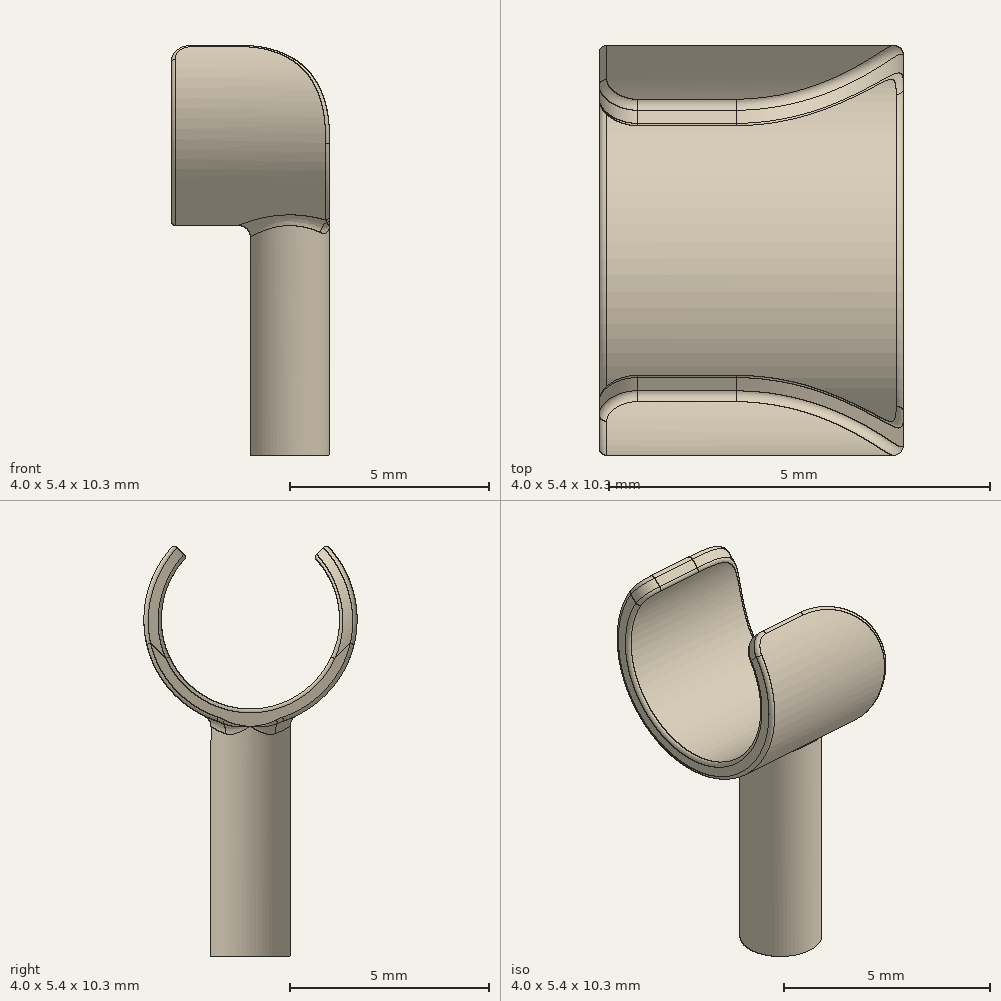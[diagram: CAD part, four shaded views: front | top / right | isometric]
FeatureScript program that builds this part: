
annotation { "Feature Type Name" : "Feature", "Feature Type Description" : "" }
export const myFeature = defineFeature(function(context is Context, id is Id, definition is map)
    precondition{}
    {
        {
            var Q0;
            Q0=qCreatedBy(makeId("Top.planeOp"),FACE);
            var sketch = newSketch(context, id + "F0", { "sketchPlane" : qUnion([Q0])});
            skCircle(sketch, "E0", {"center": v(0, 0) * mm, "radius": 1 * mm});
            skSolve(sketch);
        }
        {
            var Q0;
            Q0=makeQuery(id+"F0.imprint","IMPRINT",FACE,{"disambiguationData":[TD([[makeQuery(id+"F0.imprint","IMPRINT",EDGE,{"derivedFrom":sQuery(id+"F0.wireOp",EDGE,"E0")}),1.0]])]});
            extrude(context, id + "F1", {"entities" : qUnion([Q0]), "depth" : 6 * mm});
        }
        {
            var Q0;
            Q0=qCreatedBy(makeId("Right.planeOp"),FACE);
            cPlane(context, id + "F2", {"entities" : qUnion([Q0]), "cplaneType" : CPlaneType.OFFSET, "offset" : 1 * mm, "width" : 150 * mm, "height" : 150 * mm});
        }
        {
            var Q0;
            Q0=qCreatedBy(id+"F2.planeOp",FACE);
            var sketch = newSketch(context, id + "F3", { "sketchPlane" : qUnion([Q0])});
            skArc(sketch, "E1", {"start": v(-1.6, 10.67) * mm, "mid": v(0, 5.8) * mm, "end": v(1.6, 10.67) * mm});
            skArc(sketch, "E2", {"start": v(-1.6, 10.08) * mm, "mid": v(0, 6.25) * mm, "end": v(1.6, 10.08) * mm});
            skLineSegment(sketch, "E3.0", {"start": v(-1, 6) * mm, "end": v(1, 6) * mm});
            skLineSegment(sketch, "E4", {"start": v(0, 8.5) * mm, "end": v(-2.59, 11.06) * mm});
            skLineSegment(sketch, "E5", {"start": v(0, 8.5) * mm, "end": v(2.69, 11.16) * mm});
            skLineSegment(sketch, "E6", {"start": v(1.6, 10.08) * mm, "end": v(1.6, 10.67) * mm});
            skLineSegment(sketch, "E7", {"start": v(-1.6, 10.08) * mm, "end": v(-1.6, 10.67) * mm});
            skSolve(sketch);
        }
        {
            var Q0;
            {var subQ0=sQuery(id+"F3.wireOp",EDGE,"E2");Q0=makeQuery(id+"F3.imprint","IMPRINT",FACE,{"disambiguationData":[TD([[makeQuery(id+"F3.imprint","IMPRINT",EDGE,{"derivedFrom":subQ0}),-1.0]])]});}
            var Q1;
            {var subQ0=sQuery(id+"F3.wireOp",EDGE,"E3.0");Q1=makeQuery(id+"F3.imprint","IMPRINT",FACE,{"disambiguationData":[TD([[makeQuery(id+"F3.imprint","IMPRINT",EDGE,{"derivedFrom":subQ0}),-1.0]])]});}
            extrude(context, id + "F4", {"entities" : qUnion([Q0, Q1]), "operationType" : NewBodyOperationType.ADD, "oppositeDirection" : true, "depth" : 4 * mm});
        }
        {
            var Q0;
            Q0=makeQuery(id+"F4.boolean.opBoolean","INTERSECT",EDGE,{"derivedFrom":[makeQuery(id+"F1.opExtrude","SWEPT_FACE",FACE,{"disambiguationData":[OSD([sQuery(id+"F0.wireOp",EDGE,"E0")])]}),makeQuery(id+"F4.opExtrude","SWEPT_FACE",FACE,{"disambiguationData":[OSD([sQuery(id+"F3.wireOp",EDGE,"E1")])]})]});
            fillet(context, id + "F5", {"entities" : qUnion([Q0]), "radius" : 0.3 * mm, "tangentPropagation" : true, "allowEdgeOverflow" : false});
        }
        {
            var Q0;
            Q0=makeQuery(id+"F4.opExtrude","CAP_EDGE",EDGE,{"disambiguationData":[OSD([sQuery(id+"F3.wireOp",EDGE,"E4")])],"isStart":true});
            var Q1;
            Q1=makeQuery(id+"F4.opExtrude","CAP_EDGE",EDGE,{"disambiguationData":[OSD([sQuery(id+"F3.wireOp",EDGE,"E5")])],"isStart":true});
            fillet(context, id + "F6", {"entities" : qUnion([Q0, Q1]), "radius" : 2.2 * mm, "tangentPropagation" : true, "allowEdgeOverflow" : false});
        }
        {
            var Q0;
            Q0=makeQuery(id+"F4.opExtrude","CAP_EDGE",EDGE,{"disambiguationData":[OSD([sQuery(id+"F3.wireOp",EDGE,"E5")])],"isStart":false});
            var Q1;
            Q1=makeQuery(id+"F4.opExtrude","CAP_EDGE",EDGE,{"disambiguationData":[OSD([sQuery(id+"F3.wireOp",EDGE,"E4")])],"isStart":false});
            fillet(context, id + "F7", {"entities" : qUnion([Q0, Q1]), "radius" : 0.5 * mm, "tangentPropagation" : true, "allowEdgeOverflow" : false});
        }
        {
            var Q0;
            Q0=makeQuery(id+"F4.opExtrude","CAP_EDGE",EDGE,{"disambiguationData":[OSD([sQuery(id+"F3.wireOp",EDGE,"E2")])],"isStart":false});
            var Q1;
            Q1=makeQuery(id+"F4.opExtrude","CAP_EDGE",EDGE,{"disambiguationData":[OSD([sQuery(id+"F3.wireOp",EDGE,"E1")])],"isStart":false});
            fillet(context, id + "F8", {"entities" : qUnion([Q0, Q1]), "radius" : 0.1 * mm, "tangentPropagation" : true, "allowEdgeOverflow" : false});
        }
    });
